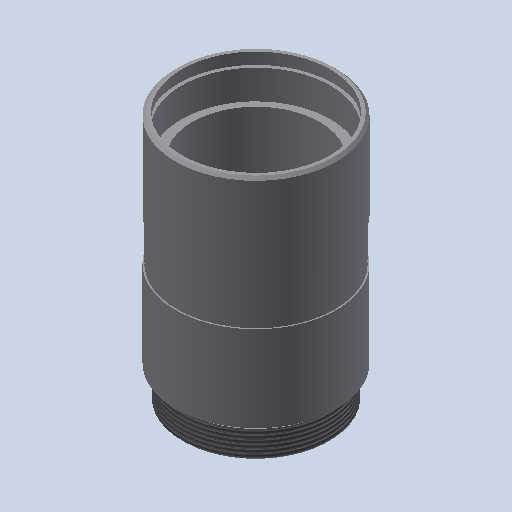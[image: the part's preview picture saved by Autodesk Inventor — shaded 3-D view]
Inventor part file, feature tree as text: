
AUTODESK INVENTOR PART (.ipt)
format: ipt  version: 2022 (Build 260153000, 153)  size: 256,512 bytes
history: native  units: mm
features: plane x10, sketch x10, extrude x7, hole x3, chamfer x3, other x2, thread x1
ambient origin geometry x8: Origin, YZ Plane, XZ Plane, XY Plane, X Axis, Y Axis, Z Axis, Center Point
bodies: Volumenkörper1 (feature_tree)
feature tree (36):
  other  "Nut"
  extrude  "Extrusion1"  Depth=93.0mm TaperAngle=0.0deg
  plane  "Arbeitsebene1"
  plane  "Arbeitsebene2"
  plane  "Arbeitsebene11"
  extrude  "Extrusion9"  [1 undecoded]
  hole  "Bohrung1"  [1 undecoded]
  plane  "Arbeitsebene13"
  hole  "Bohrung2"  [1 undecoded]
  hole  "Bohrung3"  [1 undecoded]
  extrude  "Extrusion3"  Depth=10.0mm TaperAngle=0.0deg
  plane  "Arbeitsebene4"
  sketch  "Skizze7"  dims[d36=12.0mm d37=0.0mm d38=2.0mm]
  plane  "Arbeitsebene5"
  extrude  "Extrusion4"  Depth=2.0mm
  thread  "Gewinde1"  [1 undecoded]
  chamfer  "Fase3"  Distance=3.0mm
  plane  "Arbeitsebene10"
  extrude  "Extrusion6"  Depth=2.0mm
  chamfer  "Fase8"  Distance=2.5mm
  other  "Nut1"
  plane  "Arbeitsebene12"
  extrude  "Extrusion7"  Depth=1.1mm TaperAngle=0.0deg
  plane  "Arbeitsebene14"
  extrude  "Extrusion8"  [1 undecoded]
  chamfer  "Fase10"  Distance=1.25mm
  sketch  "Skizze1"  dims[d0=60.0mm d1=93.0mm d2=0.0mm]
  sketch  "Skizze3"  dims[d4=-33.0mm d5=-49.0mm]
  sketch  "Skizze4"  dims[d11=55.5mm d12=6.0mm d13=4.0mm d14=2.0mm d15=90.0deg d16=15.0mm d17=0.0mm]
  sketch  "Skizze5"  dims[d18=47.5mm d19=6.0mm d20=4.0mm d21=2.0mm d22=90.0deg d23=8.0mm d24=20.594885mm]
  sketch  "Skizze6"  dims[d25=49.0mm d26=6.0mm d27=4.0mm d28=2.0mm d29=90.0deg d30=43.0mm d31=0.0mm d35=55.0mm]
  plane  "Arbeitsebene9"
  sketch  "Skizze9"  dims[d39=53.2mm d40=0.0mm]
  sketch  "Skizze10"  dims[d41=12.0mm d42=0.0mm d43=10.0mm d44=0.0mm]
  sketch  "Skizze11"  dims[d45=0.5mm d46=2.0mm d47=45.0deg d65=2.0mm d66=2.9mm d67=51.2mm d68=3.0mm d69=0.0mm]
  sketch  "Skizze12"  dims[d73=1.0mm d74=2.0mm d75=45.0deg d76=1.5mm d77=2.5mm d79=1.1mm d80=0.0mm d81=-5.2mm d82=1.25mm d83=2.4mm d84=0.0mm d89=10.0mm d90=0.0mm d91=0.5mm d92=1.0mm d93=2.0mm d94=45.0deg]
note: 6 required parameter values undecoded (feature->parameter linkage not recoverable at this tier; creation-order binding heuristic only, values carry confidence <= 0.55)
